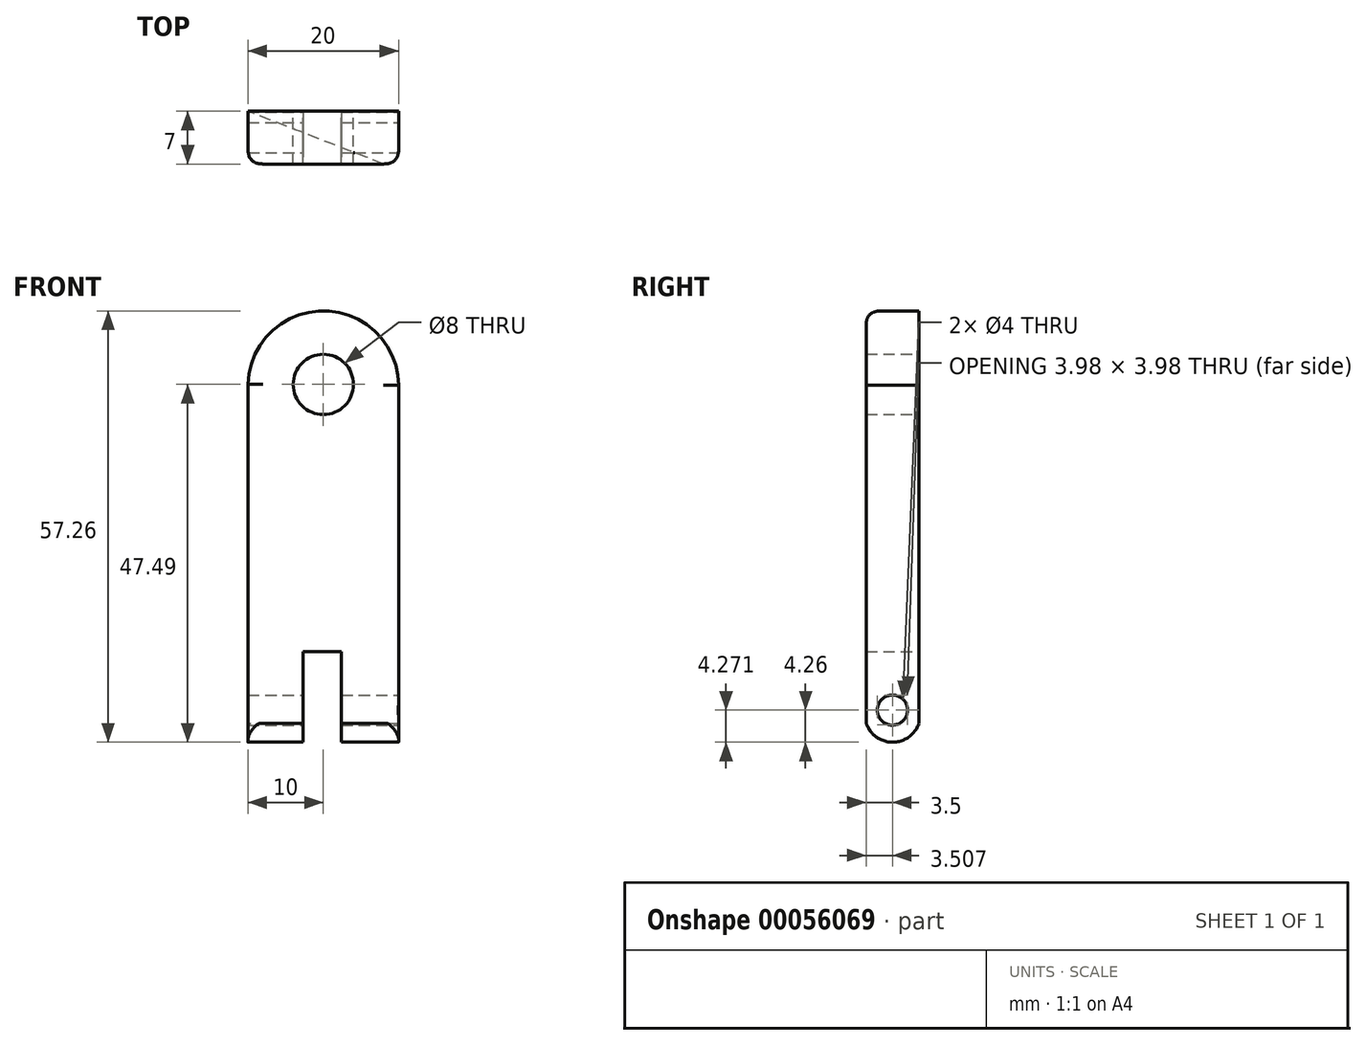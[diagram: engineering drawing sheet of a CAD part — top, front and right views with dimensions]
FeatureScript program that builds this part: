
annotation { "Feature Type Name" : "Feature", "Feature Type Description" : "" }
export const myFeature = defineFeature(function(context is Context, id is Id, definition is map)
    precondition{}
    {
        {
            var Q0;
            Q0=qCreatedBy(makeId("Front.planeOp"),FACE);
            var sketch = newSketch(context, id + "F0", { "sketchPlane" : qUnion([Q0])});
            skLineSegment(sketch, "E0.bottom", {"start": v(0, 54.73) * mm, "end": v(20, 54.73) * mm});
            skLineSegment(sketch, "E0.top", {"start": v(0, -5.27) * mm, "end": v(20, -5.27) * mm});
            skLineSegment(sketch, "E0.left", {"start": v(0, 54.73) * mm, "end": v(0, -5.27) * mm});
            skLineSegment(sketch, "E0.right", {"start": v(20, 54.73) * mm, "end": v(20, -5.27) * mm});
            skCircle(sketch, "E1", {"center": v(10, 39.73) * mm, "radius": 4 * mm});
            skArc(sketch, "E2", {"start": v(20, 39.37) * mm, "mid": v(10.21, 49.5) * mm, "end": v(0, 39.79) * mm});
            skSolve(sketch);
        }
        {
            var Q0;
            {var subQ1=sQuery(id+"F0.wireOp",EDGE,"E0.top");Q0=makeQuery(id+"F0.imprint","IMPRINT",FACE,{"disambiguationData":[TD([[makeQuery(id+"F0.imprint","IMPRINT",EDGE,{"derivedFrom":subQ1}),1.0]])]});}
            extrude(context, id + "F1", {"entities" : qUnion([Q0]), "depth" : 7 * mm});
        }
        {
            var Q0;
            Q0=qCreatedBy(makeId("Right.planeOp"),FACE);
            var sketch = newSketch(context, id + "F2", { "sketchPlane" : qUnion([Q0])});
            skArc(sketch, "E3", {"start": v(-7, -5.17) * mm, "mid": v(-3.55, -7.76) * mm, "end": v(0, -5.3) * mm});
            skLineSegment(sketch, "E4", {"start": v(-7, -5.17) * mm, "end": v(-3.48, -4.07) * mm});
            skLineSegment(sketch, "E5", {"start": v(0, -5.3) * mm, "end": v(-3.48, -4.07) * mm});
            skSolve(sketch);
        }
        {
            var Q0;
            Q0 = qSketchRegion(id + "F2", true);
            extrude(context, id + "F3", {"entities" : qUnion([Q0]), "operationType" : NewBodyOperationType.ADD, "depth" : 20 * mm});
        }
        {
            var Q0;
            Q0=makeQuery(id+"F1.opExtrude","CAP_FACE",FACE,{"disambiguationData":[OSD([sQuery(id+"F0.wireOp",EDGE,"E0.bottom"),sQuery(id+"F0.wireOp",EDGE,"E0.top"),sQuery(id+"F0.wireOp",EDGE,"E0.left"),sQuery(id+"F0.wireOp",EDGE,"E0.right"),sQuery(id+"F0.wireOp",EDGE,"E1")])],"isStart":true});
            var sketch = newSketch(context, id + "F4", { "sketchPlane" : qUnion([Q0])});
            skLineSegment(sketch, "E6.bottom", {"start": v(-12.4, -11.3) * mm, "end": v(-7.3, -11.3) * mm});
            skLineSegment(sketch, "E6.top", {"start": v(-12.4, 4.23) * mm, "end": v(-7.3, 4.23) * mm});
            skLineSegment(sketch, "E6.left", {"start": v(-12.4, -11.3) * mm, "end": v(-12.4, 4.23) * mm});
            skLineSegment(sketch, "E6.right", {"start": v(-7.3, -11.3) * mm, "end": v(-7.3, 4.23) * mm});
            skSolve(sketch);
        }
        {
            var Q0;
            Q0 = qSketchRegion(id + "F4", true);
            extrude(context, id + "F5", {"entities" : qUnion([Q0]), "operationType" : NewBodyOperationType.REMOVE, "oppositeDirection" : true, "depth" : 25 * mm});
        }
        {
            var Q0;
            Q0=makeQuery(id+"F3.boolean.opBoolean","MERGE",FACE,{"derivedFrom":[makeQuery(id+"F1.opExtrude","SWEPT_FACE",FACE,{"disambiguationData":[OSD([sQuery(id+"F0.wireOp",EDGE,"E0.right")])]}),makeQuery(id+"F3.opExtrude","CAP_FACE",FACE,{"disambiguationData":[OSD([sQuery(id+"F2.wireOp",EDGE,"E3"),sQuery(id+"F2.wireOp",EDGE,"E4"),sQuery(id+"F2.wireOp",EDGE,"E5")])],"isStart":false})]});
            var sketch = newSketch(context, id + "F6", { "sketchPlane" : qUnion([Q0])});
            skCircle(sketch, "E7", {"center": v(-3.5, -3.5) * mm, "radius": 2 * mm});
            skSolve(sketch);
        }
        {
            var Q0;
            Q0 = qSketchRegion(id + "F6", true);
            extrude(context, id + "F7", {"entities" : qUnion([Q0]), "operationType" : NewBodyOperationType.REMOVE, "oppositeDirection" : true, "depth" : 25 * mm});
        }
        {
            var Q0;
            Q0=makeQuery(id+"F1.opExtrude","CAP_EDGE",EDGE,{"disambiguationData":[OSD([sQuery(id+"F0.wireOp",EDGE,"E0.left")])],"isStart":false});
            var Q1;
            Q1=makeQuery(id+"F1.opExtrude","CAP_EDGE",EDGE,{"disambiguationData":[OSD([sQuery(id+"F0.wireOp",EDGE,"E0.right")])],"isStart":false});
            var Q2;
            Q2=makeQuery(id+"F1.opExtrude","CAP_EDGE",EDGE,{"disambiguationData":[OSD([sQuery(id+"F0.wireOp",EDGE,"E2")])],"isStart":false});
            fillet(context, id + "F8", {"entities" : qUnion([Q0, Q1, Q2]), "radius" : 2 * mm, "tangentPropagation" : true, "rho" : 0.5, "crossSection" : FilletCrossSection.CONIC, "allowEdgeOverflow" : false});
        }
    });
